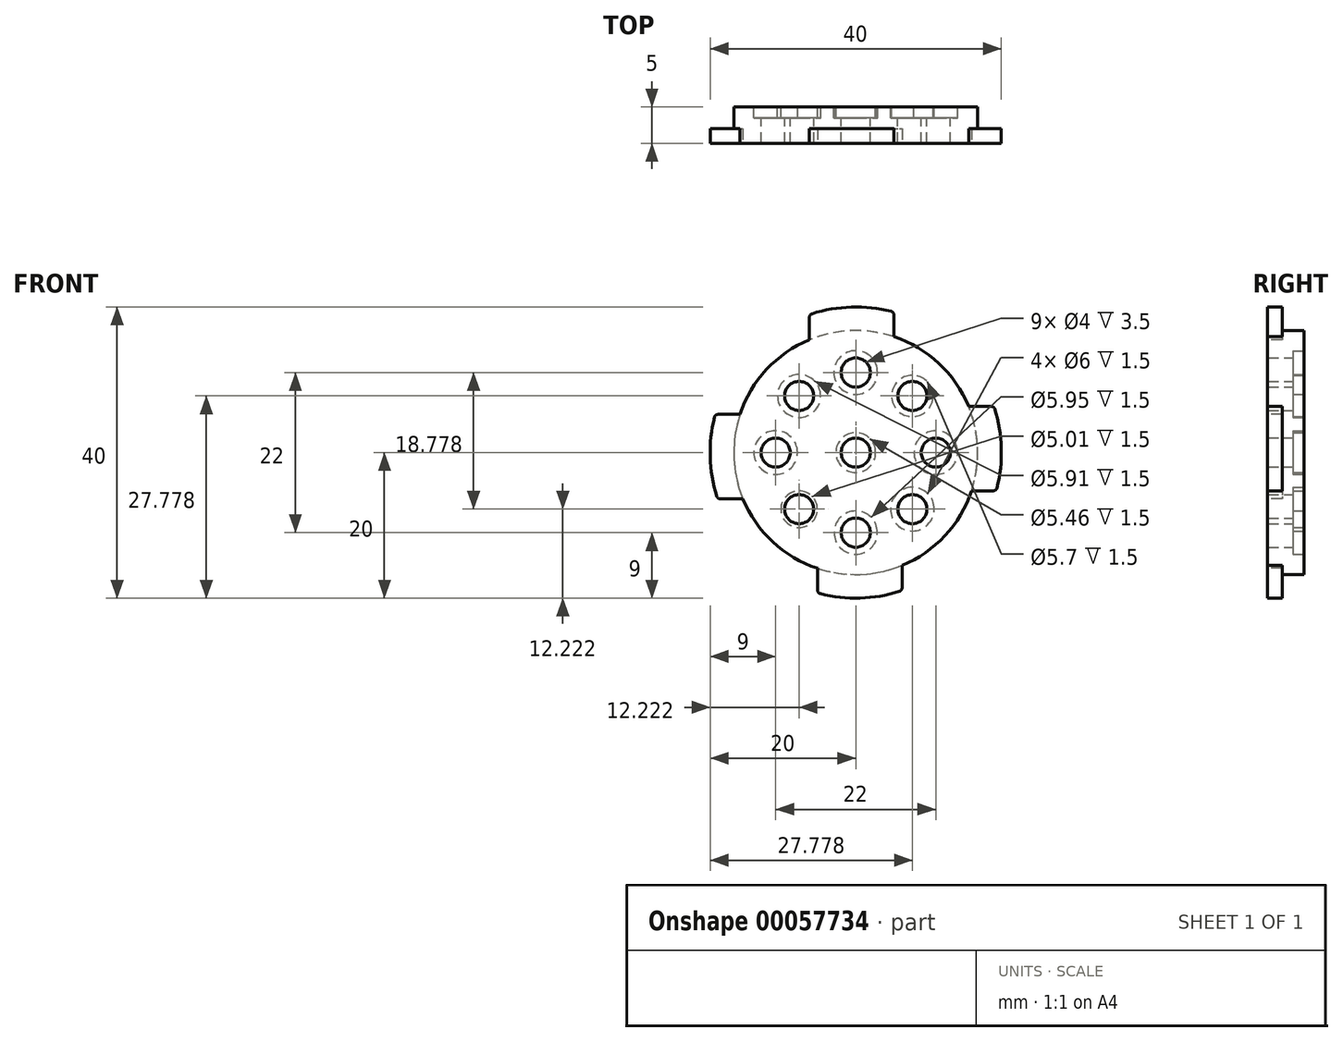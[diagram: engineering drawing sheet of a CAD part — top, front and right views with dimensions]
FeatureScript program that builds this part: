
annotation { "Feature Type Name" : "Feature", "Feature Type Description" : "" }
export const myFeature = defineFeature(function(context is Context, id is Id, definition is map)
    precondition{}
    {
        {
            var Q0;
            Q0=qCreatedBy(makeId("Front.planeOp"),FACE);
            var sketch = newSketch(context, id + "F0", { "sketchPlane" : qUnion([Q0])});
            skCircle(sketch, "E0", {"center": v(0, 0) * mm, "radius": 16.75 * mm});
            skSolve(sketch);
        }
        {
            var Q0;
            Q0 = qSketchRegion(id + "F0", true);
            extrude(context, id + "F1", {"entities" : qUnion([Q0]), "depth" : 5 * mm});
        }
        {
            var Q0;
            Q0=makeQuery(id+"F1.opExtrude","CAP_FACE",FACE,{"disambiguationData":[OSD([sQuery(id+"F0.wireOp",EDGE,"E0")])],"isStart":false});
            var sketch = newSketch(context, id + "F2", { "sketchPlane" : qUnion([Q0])});
            skArc(sketch, "E1", {"start": v(5.24, 19.3) * mm, "mid": v(-0.58, 20) * mm, "end": v(-6.36, 18.96) * mm});
            skLineSegment(sketch, "E2", {"start": v(5.24, 19.3) * mm, "end": v(5.24, 15.9) * mm});
            skLineSegment(sketch, "E3", {"start": v(-6.36, 18.96) * mm, "end": v(-6.36, 15.5) * mm});
            skCircle(sketch, "E4.0", {"center": v(0, 0) * mm, "radius": 16.75 * mm});
            skLineSegment(sketch, "E5.1.0", {"start": v(-19.3, 5.24) * mm, "end": v(-15.9, 5.24) * mm});
            skArc(sketch, "E5.1.1", {"start": v(-19.3, 5.24) * mm, "mid": v(-20, -0.58) * mm, "end": v(-18.96, -6.36) * mm});
            skLineSegment(sketch, "E5.1.2", {"start": v(-18.96, -6.36) * mm, "end": v(-15.5, -6.36) * mm});
            skLineSegment(sketch, "E5.2.0", {"start": v(-5.24, -19.3) * mm, "end": v(-5.24, -15.9) * mm});
            skArc(sketch, "E5.2.1", {"start": v(-5.24, -19.3) * mm, "mid": v(0.58, -20) * mm, "end": v(6.36, -18.96) * mm});
            skLineSegment(sketch, "E5.2.2", {"start": v(6.36, -18.96) * mm, "end": v(6.36, -15.5) * mm});
            skLineSegment(sketch, "E5.3.0", {"start": v(19.3, -5.24) * mm, "end": v(15.9, -5.24) * mm});
            skArc(sketch, "E5.3.1", {"start": v(19.3, -5.24) * mm, "mid": v(20, 0.58) * mm, "end": v(18.96, 6.36) * mm});
            skLineSegment(sketch, "E5.3.2", {"start": v(18.96, 6.36) * mm, "end": v(15.5, 6.36) * mm});
            skSolve(sketch);
        }
        {
            var Q0;
            Q0 = qSketchRegion(id + "F2", true);
            extrude(context, id + "F3", {"entities" : qUnion([Q0]), "operationType" : NewBodyOperationType.ADD, "oppositeDirection" : true, "depth" : 2 * mm});
        }
        {
            var Q0;
            Q0=makeQuery(id+"F1.opExtrude","CAP_FACE",FACE,{"disambiguationData":[OSD([sQuery(id+"F0.wireOp",EDGE,"E0")])],"isStart":true});
            var sketch = newSketch(context, id + "F4", { "sketchPlane" : qUnion([Q0])});
            skCircle(sketch, "E6", {"center": v(0, 0) * mm, "radius": 2 * mm});
            skCircle(sketch, "E7", {"center": v(0, 0) * mm, "radius": 11 * mm, "construction": true});
            skCircle(sketch, "E8", {"center": v(0, 11) * mm, "radius": 2 * mm});
            skCircle(sketch, "E9.1.0", {"center": v(-7.78, 7.78) * mm, "radius": 2 * mm});
            skCircle(sketch, "E9.2.0", {"center": v(-11, 0) * mm, "radius": 2 * mm});
            skCircle(sketch, "E9.3.0", {"center": v(-7.78, -7.78) * mm, "radius": 2 * mm});
            skCircle(sketch, "E9.4.0", {"center": v(0, -11) * mm, "radius": 2 * mm});
            skCircle(sketch, "E9.5.0", {"center": v(7.78, -7.78) * mm, "radius": 2 * mm});
            skCircle(sketch, "E9.6.0", {"center": v(11, 0) * mm, "radius": 2 * mm});
            skCircle(sketch, "E9.7.0", {"center": v(7.78, 7.78) * mm, "radius": 2 * mm});
            skSolve(sketch);
        }
        {
            var Q0;
            Q0=makeQuery(id+"F4.imprint","IMPRINT",FACE,{"disambiguationData":[TD([[makeQuery(id+"F4.imprint","IMPRINT",EDGE,{"derivedFrom":sQuery(id+"F4.wireOp",EDGE,"E9.1.0")}),1.0]])]});
            var Q1;
            Q1=makeQuery(id+"F4.imprint","IMPRINT",FACE,{"disambiguationData":[TD([[makeQuery(id+"F4.imprint","IMPRINT",EDGE,{"derivedFrom":sQuery(id+"F4.wireOp",EDGE,"E9.2.0")}),1.0]])]});
            var Q2;
            Q2=makeQuery(id+"F4.imprint","IMPRINT",FACE,{"disambiguationData":[TD([[makeQuery(id+"F4.imprint","IMPRINT",EDGE,{"derivedFrom":sQuery(id+"F4.wireOp",EDGE,"E9.3.0")}),1.0]])]});
            var Q3;
            Q3=makeQuery(id+"F4.imprint","IMPRINT",FACE,{"disambiguationData":[TD([[makeQuery(id+"F4.imprint","IMPRINT",EDGE,{"derivedFrom":sQuery(id+"F4.wireOp",EDGE,"E9.4.0")}),1.0]])]});
            var Q4;
            Q4=makeQuery(id+"F4.imprint","IMPRINT",FACE,{"disambiguationData":[TD([[makeQuery(id+"F4.imprint","IMPRINT",EDGE,{"derivedFrom":sQuery(id+"F4.wireOp",EDGE,"E9.5.0")}),1.0]])]});
            var Q5;
            Q5=makeQuery(id+"F4.imprint","IMPRINT",FACE,{"disambiguationData":[TD([[makeQuery(id+"F4.imprint","IMPRINT",EDGE,{"derivedFrom":sQuery(id+"F4.wireOp",EDGE,"E9.6.0")}),1.0]])]});
            var Q6;
            Q6=makeQuery(id+"F4.imprint","IMPRINT",FACE,{"disambiguationData":[TD([[makeQuery(id+"F4.imprint","IMPRINT",EDGE,{"derivedFrom":sQuery(id+"F4.wireOp",EDGE,"E9.7.0")}),1.0]])]});
            var Q7;
            Q7=makeQuery(id+"F4.imprint","IMPRINT",FACE,{"disambiguationData":[TD([[makeQuery(id+"F4.imprint","IMPRINT",EDGE,{"derivedFrom":sQuery(id+"F4.wireOp",EDGE,"E6")}),1.0]])]});
            var Q8;
            Q8=makeQuery(id+"F4.imprint","IMPRINT",FACE,{"disambiguationData":[TD([[makeQuery(id+"F4.imprint","IMPRINT",EDGE,{"derivedFrom":sQuery(id+"F4.wireOp",EDGE,"E8")}),1.0]])]});
            extrude(context, id + "F5", {"entities" : qUnion([Q0, Q1, Q2, Q3, Q4, Q5, Q6, Q7, Q8]), "operationType" : NewBodyOperationType.REMOVE, "endBound" : BoundingType.UP_TO_NEXT, "oppositeDirection" : true, "depth" : 25 * mm});
        }
        {
            var Q0;
            Q0=makeQuery(id+"F1.opExtrude","CAP_FACE",FACE,{"disambiguationData":[OSD([sQuery(id+"F0.wireOp",EDGE,"E0")])],"isStart":true});
            var sketch = newSketch(context, id + "F6", { "sketchPlane" : qUnion([Q0])});
            skCircle(sketch, "E10", {"center": v(-7.78, 7.78) * mm, "radius": 2.85 * mm});
            skCircle(sketch, "E11", {"center": v(-11, 0) * mm, "radius": 3 * mm});
            skCircle(sketch, "E12", {"center": v(-7.78, -7.78) * mm, "radius": 3 * mm});
            skCircle(sketch, "E13", {"center": v(0, -11) * mm, "radius": 2.98 * mm});
            skCircle(sketch, "E14", {"center": v(7.78, -7.78) * mm, "radius": 2.5 * mm});
            skCircle(sketch, "E15", {"center": v(11, 0) * mm, "radius": 3 * mm});
            skCircle(sketch, "E16", {"center": v(0, 0) * mm, "radius": 2.73 * mm});
            skCircle(sketch, "E17", {"center": v(7.78, 7.78) * mm, "radius": 2.96 * mm});
            skCircle(sketch, "E18", {"center": v(0, 11) * mm, "radius": 3 * mm});
            skSolve(sketch);
        }
        {
            var Q0;
            Q0 = qSketchRegion(id + "F6", true);
            extrude(context, id + "F7", {"entities" : qUnion([Q0]), "operationType" : NewBodyOperationType.REMOVE, "oppositeDirection" : true, "depth" : 1.5 * mm});
        }
        {
            var Q0;
            Q0=makeQuery(id+"F3.opExtrude","SWEPT_EDGE",EDGE,{"disambiguationData":[OSD([sQuery(id+"F2.wireOp",EDGE,"E1"),sQuery(id+"F2.wireOp",EDGE,"E2")])]});
            var Q1;
            Q1=makeQuery(id+"F3.opExtrude","SWEPT_EDGE",EDGE,{"disambiguationData":[OSD([sQuery(id+"F2.wireOp",EDGE,"E1"),sQuery(id+"F2.wireOp",EDGE,"E3")])]});
            var Q2;
            Q2=makeQuery(id+"F3.opExtrude","SWEPT_EDGE",EDGE,{"disambiguationData":[OSD([sQuery(id+"F2.wireOp",EDGE,"E5.3.1"),sQuery(id+"F2.wireOp",EDGE,"E5.3.2")])]});
            var Q3;
            Q3=makeQuery(id+"F3.opExtrude","SWEPT_EDGE",EDGE,{"disambiguationData":[OSD([sQuery(id+"F2.wireOp",EDGE,"E5.1.0"),sQuery(id+"F2.wireOp",EDGE,"E5.1.1")])]});
            var Q4;
            Q4=makeQuery(id+"F3.opExtrude","SWEPT_EDGE",EDGE,{"disambiguationData":[OSD([sQuery(id+"F2.wireOp",EDGE,"E5.3.0"),sQuery(id+"F2.wireOp",EDGE,"E5.3.1")])]});
            var Q5;
            Q5=makeQuery(id+"F3.opExtrude","SWEPT_EDGE",EDGE,{"disambiguationData":[OSD([sQuery(id+"F2.wireOp",EDGE,"E5.1.1"),sQuery(id+"F2.wireOp",EDGE,"E5.1.2")])]});
            var Q6;
            Q6=makeQuery(id+"F3.opExtrude","SWEPT_EDGE",EDGE,{"disambiguationData":[OSD([sQuery(id+"F2.wireOp",EDGE,"E5.2.1"),sQuery(id+"F2.wireOp",EDGE,"E5.2.2")])]});
            var Q7;
            Q7=makeQuery(id+"F3.opExtrude","SWEPT_EDGE",EDGE,{"disambiguationData":[OSD([sQuery(id+"F2.wireOp",EDGE,"E5.2.0"),sQuery(id+"F2.wireOp",EDGE,"E5.2.1")])]});
            fillet(context, id + "F8", {"entities" : qUnion([Q0, Q1, Q2, Q3, Q4, Q5, Q6, Q7]), "radius" : .5 * mm, "tangentPropagation" : true, "allowEdgeOverflow" : false});
        }
    });
